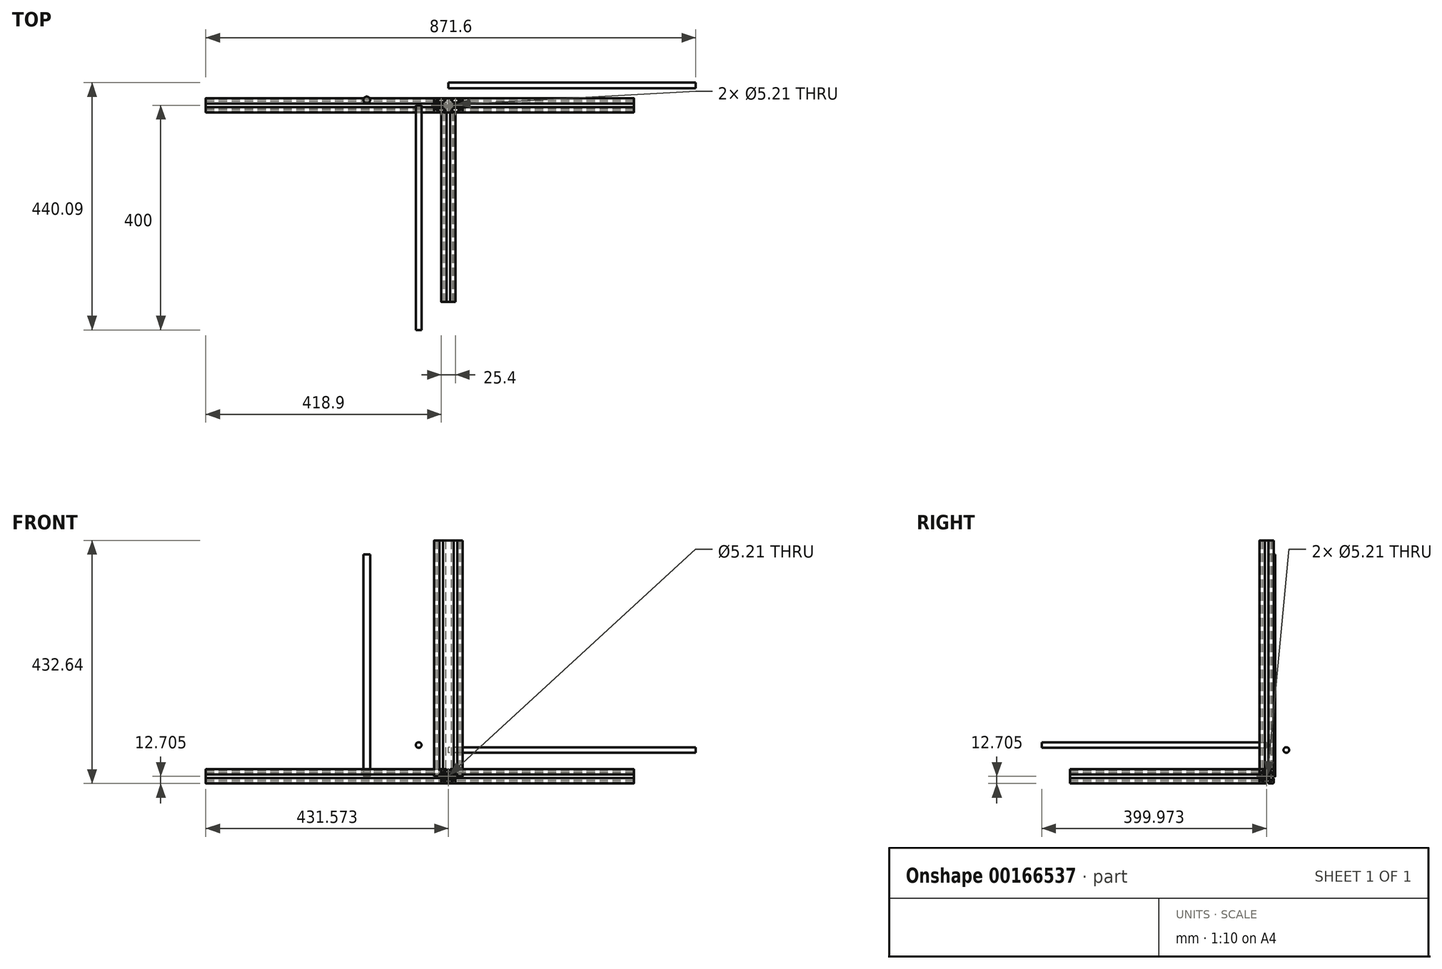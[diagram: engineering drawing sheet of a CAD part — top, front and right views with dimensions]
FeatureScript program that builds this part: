
annotation { "Feature Type Name" : "Feature", "Feature Type Description" : "" }
export const myFeature = defineFeature(function(context is Context, id is Id, definition is map)
    precondition{}
    {
        {
            assignVariable(context, id + "F0", {"name" : "Y_Extrusion_Length", "anyValue" : 350});
        }
        {
            assignVariable(context, id + "F1", {"name" : "X_Extrusion_Length", "anyValue" : 330});
        }
        {
            assignVariable(context, id + "F2", {"name" : "Z_Extrusion_Length", "anyValue" : 420});
        }
        {
            assignVariable(context, id + "F3", {"name" : "Y_Rod_Length", "anyValue" : 440});
        }
        {
            assignVariable(context, id + "F4", {"name" : "ZX_Extrusion_Length", "anyValue" : getVariable(context, 'X_Extrusion_Length') + 25.4 * 4});
        }
        {
            var Q0;
            Q0=qCreatedBy(makeId("Front.planeOp"),FACE);
            var sketch = newSketch(context, id + "F5", { "sketchPlane" : qUnion([Q0])});
            skArc(sketch, "E0", {"start": v(-10.62, 12.76) * mm, "mid": v(-12.1, 12.15) * mm, "end": v(-12.73, 10.66) * mm});
            skArc(sketch, "E1", {"start": v(-12.73, 4.4) * mm, "mid": v(-11.62, 3.3) * mm, "end": v(-10.52, 4.4) * mm});
            skArc(sketch, "E2", {"start": v(-4.37, 10.55) * mm, "mid": v(-3.27, 11.66) * mm, "end": v(-4.37, 12.76) * mm});
            skArc(sketch, "E3", {"start": v(-8.75, 7.2) * mm, "mid": v(-9.88, 7.42) * mm, "end": v(-10.52, 6.46) * mm});
            skArc(sketch, "E4", {"start": v(-6.43, 10.55) * mm, "mid": v(-7.38, 9.92) * mm, "end": v(-7.16, 8.8) * mm});
            skLineSegment(sketch, "E5", {"start": v(-12.73, 10.66) * mm, "end": v(-12.73, 4.4) * mm});
            skLineSegment(sketch, "E6", {"start": v(-10.62, 12.76) * mm, "end": v(-4.37, 12.76) * mm});
            skLineSegment(sketch, "E7", {"start": v(-10.52, 4.4) * mm, "end": v(-10.52, 6.46) * mm});
            skLineSegment(sketch, "E8", {"start": v(-4.37, 10.55) * mm, "end": v(-6.43, 10.55) * mm});
            skLineSegment(sketch, "E9", {"start": v(-11.51, 7.5) * mm, "end": v(-10.3, 7.5) * mm, "construction": true});
            skLineSegment(sketch, "E10", {"start": v(-13.64, 3.3) * mm, "end": v(-12.36, 3.3) * mm, "construction": true});
            skLineSegment(sketch, "E11", {"start": v(-7.46, 11.03) * mm, "end": v(-7.46, 8.91) * mm, "construction": true});
            skLineSegment(sketch, "E12", {"start": v(-3.27, 12.37) * mm, "end": v(-3.27, 10.25) * mm, "construction": true});
            skLineSegment(sketch, "E13.bottom", {"start": v(1.57, 4.57) * mm, "end": v(-1.63, 4.57) * mm});
            skLineSegment(sketch, "E13.top", {"start": v(1.57, -4.44) * mm, "end": v(-1.63, -4.44) * mm});
            skLineSegment(sketch, "E13.left", {"start": v(4.48, 1.66) * mm, "end": v(4.48, -1.53) * mm});
            skLineSegment(sketch, "E13.right", {"start": v(-4.54, 1.66) * mm, "end": v(-4.54, -1.53) * mm});
            skPoint(sketch, "E13.middle", {"position": v(-0.03, 0.06) * mm});
            skLineSegment(sketch, "E14", {"start": v(-8.75, 7.2) * mm, "end": v(-5.47, 3.9) * mm});
            skLineSegment(sketch, "E15", {"start": v(-7.16, 8.8) * mm, "end": v(-3.87, 5.5) * mm});
            skArc(sketch, "E16.filletArc", {"start": v(-3.87, 5.5) * mm, "mid": v(-2.84, 4.81) * mm, "end": v(-1.63, 4.57) * mm});
            skArc(sketch, "E17.filletArc", {"start": v(-4.54, 1.66) * mm, "mid": v(-4.78, 2.88) * mm, "end": v(-5.47, 3.9) * mm});
            skLineSegment(sketch, "E18", {"start": v(5.32, 0.06) * mm, "end": v(-7.21, 0.06) * mm, "construction": true});
            skPoint(sketch, "E18.startSnap0", {"position": v(2.97, 0.06) * mm});
            skPoint(sketch, "E19", {"position": v(-0.03, -4.44) * mm});
            skLineSegment(sketch, "E20", {"start": v(-0.03, -6.76) * mm, "end": v(-0.03, 5.83) * mm, "construction": true});
            skLineSegment(sketch, "E21.MirrorCS", {"start": v(11.46, 7.5) * mm, "end": v(10.25, 7.5) * mm, "construction": true});
            skArc(sketch, "E22.MirrorCS", {"start": v(10.57, 12.76) * mm, "mid": v(12.06, 12.15) * mm, "end": v(12.67, 10.66) * mm});
            skLineSegment(sketch, "E23.MirrorCS", {"start": v(7.4, 11.03) * mm, "end": v(7.4, 8.91) * mm, "construction": true});
            skLineSegment(sketch, "E24.MirrorCS", {"start": v(10.46, 4.4) * mm, "end": v(10.46, 6.46) * mm});
            skArc(sketch, "E25.MirrorCS", {"start": v(3.82, 5.5) * mm, "mid": v(2.79, 4.81) * mm, "end": v(1.57, 4.57) * mm});
            skLineSegment(sketch, "E26.MirrorCS", {"start": v(8.7, 7.2) * mm, "end": v(5.41, 3.9) * mm});
            skLineSegment(sketch, "E27.MirrorCS", {"start": v(3.21, 12.37) * mm, "end": v(3.21, 10.25) * mm, "construction": true});
            skLineSegment(sketch, "E28.MirrorCS", {"start": v(13.58, 3.3) * mm, "end": v(12.3, 3.3) * mm, "construction": true});
            skArc(sketch, "E29.MirrorCS", {"start": v(4.32, 10.55) * mm, "mid": v(3.21, 11.66) * mm, "end": v(4.32, 12.76) * mm});
            skArc(sketch, "E30.MirrorCS", {"start": v(8.7, 7.2) * mm, "mid": v(9.83, 7.42) * mm, "end": v(10.46, 6.46) * mm});
            skArc(sketch, "E31.MirrorCS", {"start": v(12.67, 4.4) * mm, "mid": v(11.57, 3.3) * mm, "end": v(10.46, 4.4) * mm});
            skLineSegment(sketch, "E32.MirrorCS", {"start": v(10.57, 12.76) * mm, "end": v(4.32, 12.76) * mm});
            skLineSegment(sketch, "E33.MirrorCS", {"start": v(12.67, 10.66) * mm, "end": v(12.67, 4.4) * mm});
            skArc(sketch, "E34.MirrorCS", {"start": v(6.37, 10.55) * mm, "mid": v(7.33, 9.92) * mm, "end": v(7.1, 8.8) * mm});
            skLineSegment(sketch, "E35.MirrorCS", {"start": v(7.1, 8.8) * mm, "end": v(3.82, 5.5) * mm});
            skLineSegment(sketch, "E36.MirrorCS", {"start": v(4.32, 10.55) * mm, "end": v(6.37, 10.55) * mm});
            skArc(sketch, "E37.MirrorCS", {"start": v(4.48, 1.66) * mm, "mid": v(4.72, 2.88) * mm, "end": v(5.41, 3.9) * mm});
            skLineSegment(sketch, "E38.MirrorCS", {"start": v(-11.51, -7.37) * mm, "end": v(-10.3, -7.37) * mm, "construction": true});
            skArc(sketch, "E39.MirrorCS", {"start": v(-3.87, -5.37) * mm, "mid": v(-2.84, -4.69) * mm, "end": v(-1.63, -4.44) * mm});
            skArc(sketch, "E40.MirrorCS", {"start": v(-10.62, -12.64) * mm, "mid": v(-12.1, -12.02) * mm, "end": v(-12.73, -10.53) * mm});
            skArc(sketch, "E41.MirrorCS", {"start": v(-8.75, -7.07) * mm, "mid": v(-9.88, -7.3) * mm, "end": v(-10.52, -6.33) * mm});
            skArc(sketch, "E42.MirrorCS", {"start": v(-6.43, -10.43) * mm, "mid": v(-7.38, -9.79) * mm, "end": v(-7.16, -8.66) * mm});
            skLineSegment(sketch, "E43.MirrorCS", {"start": v(-3.27, -12.24) * mm, "end": v(-3.27, -10.12) * mm, "construction": true});
            skArc(sketch, "E44.MirrorCS", {"start": v(-4.54, -1.53) * mm, "mid": v(-4.78, -2.75) * mm, "end": v(-5.47, -3.78) * mm});
            skLineSegment(sketch, "E45.MirrorCS", {"start": v(-12.73, -10.53) * mm, "end": v(-12.73, -4.28) * mm});
            skLineSegment(sketch, "E46.MirrorCS", {"start": v(-13.64, -3.17) * mm, "end": v(-12.36, -3.17) * mm, "construction": true});
            skLineSegment(sketch, "E47.MirrorCS", {"start": v(-7.46, -10.9) * mm, "end": v(-7.46, -8.78) * mm, "construction": true});
            skLineSegment(sketch, "E48.MirrorCS", {"start": v(-4.37, -10.43) * mm, "end": v(-6.43, -10.43) * mm});
            skLineSegment(sketch, "E49.MirrorCS", {"start": v(-10.62, -12.64) * mm, "end": v(-4.37, -12.64) * mm});
            skLineSegment(sketch, "E50.MirrorCS", {"start": v(-10.52, -4.28) * mm, "end": v(-10.52, -6.33) * mm});
            skArc(sketch, "E51.MirrorCS", {"start": v(-12.73, -4.28) * mm, "mid": v(-11.62, -3.17) * mm, "end": v(-10.52, -4.28) * mm});
            skLineSegment(sketch, "E52.MirrorCS", {"start": v(-8.75, -7.07) * mm, "end": v(-5.47, -3.78) * mm});
            skLineSegment(sketch, "E53.MirrorCS", {"start": v(-7.16, -8.66) * mm, "end": v(-3.87, -5.37) * mm});
            skArc(sketch, "E54.MirrorCS", {"start": v(-4.37, -10.43) * mm, "mid": v(-3.27, -11.53) * mm, "end": v(-4.37, -12.64) * mm});
            skLineSegment(sketch, "E55.MirrorCS", {"start": v(11.46, -7.37) * mm, "end": v(10.25, -7.37) * mm, "construction": true});
            skArc(sketch, "E56.MirrorCS", {"start": v(4.32, -10.43) * mm, "mid": v(3.21, -11.53) * mm, "end": v(4.32, -12.64) * mm});
            skLineSegment(sketch, "E57.MirrorCS", {"start": v(13.58, -3.17) * mm, "end": v(12.3, -3.17) * mm, "construction": true});
            skArc(sketch, "E58.MirrorCS", {"start": v(8.7, -7.07) * mm, "mid": v(9.83, -7.3) * mm, "end": v(10.46, -6.33) * mm});
            skLineSegment(sketch, "E59.MirrorCS", {"start": v(7.1, -8.66) * mm, "end": v(3.82, -5.37) * mm});
            skLineSegment(sketch, "E60.MirrorCS", {"start": v(7.4, -10.9) * mm, "end": v(7.4, -8.78) * mm, "construction": true});
            skLineSegment(sketch, "E61.MirrorCS", {"start": v(3.21, -12.24) * mm, "end": v(3.21, -10.12) * mm, "construction": true});
            skLineSegment(sketch, "E62.MirrorCS", {"start": v(4.32, -10.43) * mm, "end": v(6.37, -10.43) * mm});
            skArc(sketch, "E63.MirrorCS", {"start": v(3.82, -5.37) * mm, "mid": v(2.79, -4.69) * mm, "end": v(1.57, -4.44) * mm});
            skArc(sketch, "E64.MirrorCS", {"start": v(10.57, -12.64) * mm, "mid": v(12.06, -12.02) * mm, "end": v(12.67, -10.53) * mm});
            skLineSegment(sketch, "E65.MirrorCS", {"start": v(10.57, -12.64) * mm, "end": v(4.32, -12.64) * mm});
            skLineSegment(sketch, "E66.MirrorCS", {"start": v(8.7, -7.07) * mm, "end": v(5.41, -3.78) * mm});
            skLineSegment(sketch, "E67.MirrorCS", {"start": v(12.67, -10.53) * mm, "end": v(12.67, -4.28) * mm});
            skArc(sketch, "E68.MirrorCS", {"start": v(12.67, -4.28) * mm, "mid": v(11.57, -3.17) * mm, "end": v(10.46, -4.28) * mm});
            skArc(sketch, "E69.MirrorCS", {"start": v(4.48, -1.53) * mm, "mid": v(4.72, -2.75) * mm, "end": v(5.41, -3.78) * mm});
            skLineSegment(sketch, "E70.MirrorCS", {"start": v(10.46, -4.28) * mm, "end": v(10.46, -6.33) * mm});
            skArc(sketch, "E71.MirrorCS", {"start": v(6.37, -10.43) * mm, "mid": v(7.33, -9.79) * mm, "end": v(7.1, -8.66) * mm});
            skCircle(sketch, "E72", {"center": v(-0.03, 0.06) * mm, "radius": 2.6 * mm});
            skSolve(sketch);
        }
        {
            var Q0;
            Q0=qSketchRegion(id+"F5",true);
            extrude(context, id + "F6", {"entities" : qUnion([Q0]), "depth" : (getVariable(context, 'Y_Extrusion_Length')) * mm});
        }
        {
            var Q0;
            Q0=qCreatedBy(makeId("Top.planeOp"),FACE);
            var sketch = newSketch(context, id + "F7", { "sketchPlane" : qUnion([Q0])});
            skCircle(sketch, "E73", {"center": v(-145.13, 9.37) * mm, "radius": 6 * mm});
            skSolve(sketch);
        }
        {
            var Q0;
            Q0=makeQuery(id+"F7.imprint","IMPRINT",FACE,{"disambiguationData":[TD([[makeQuery(id+"F7.imprint","IMPRINT",EDGE,{"derivedFrom":sQuery(id+"F7.wireOp",EDGE,"E73")}),1.0]])]});
            extrude(context, id + "F8", {"entities" : qUnion([Q0]), "depth" : 395 * mm});
        }
        {
            var Q0;
            Q0=qCreatedBy(makeId("Right.planeOp"),FACE);
            var sketch = newSketch(context, id + "F9", { "sketchPlane" : qUnion([Q0])});
            skCircle(sketch, "E74", {"center": v(35.09, 47.05) * mm, "radius": 5 * mm});
            skSolve(sketch);
        }
        {
            var Q0;
            Q0=makeQuery(id+"F9.imprint","IMPRINT",FACE,{"disambiguationData":[TD([[makeQuery(id+"F9.imprint","IMPRINT",EDGE,{"derivedFrom":sQuery(id+"F9.wireOp",EDGE,"E74")}),1.0]])]});
            extrude(context, id + "F10", {"entities" : qUnion([Q0]), "depth" : (getVariable(context, 'Y_Rod_Length')) * mm});
        }
        {
            var Q0;
            Q0=qCreatedBy(makeId("Front.planeOp"),FACE);
            var sketch = newSketch(context, id + "F11", { "sketchPlane" : qUnion([Q0])});
            skCircle(sketch, "E75", {"center": v(-52.77, 55.86) * mm, "radius": 5 * mm});
            skSolve(sketch);
        }
        {
            var Q0;
            Q0=makeQuery(id+"F11.imprint","IMPRINT",FACE,{"disambiguationData":[TD([[makeQuery(id+"F11.imprint","IMPRINT",EDGE,{"derivedFrom":sQuery(id+"F11.wireOp",EDGE,"E75")}),1.0]])]});
            extrude(context, id + "F12", {"entities" : qUnion([Q0]), "depth" : 400 * mm});
        }
        {
            var Q0;
            Q0=qCreatedBy(makeId("Right.planeOp"),FACE);
            var sketch = newSketch(context, id + "F13", { "sketchPlane" : qUnion([Q0])});
            skArc(sketch, "E76", {"start": v(-10.62, 12.76) * mm, "mid": v(-12.1, 12.15) * mm, "end": v(-12.73, 10.66) * mm});
            skArc(sketch, "E77", {"start": v(-12.73, 4.4) * mm, "mid": v(-11.62, 3.3) * mm, "end": v(-10.52, 4.4) * mm});
            skArc(sketch, "E78", {"start": v(-4.37, 10.55) * mm, "mid": v(-3.27, 11.66) * mm, "end": v(-4.37, 12.76) * mm});
            skArc(sketch, "E79", {"start": v(-8.75, 7.2) * mm, "mid": v(-9.88, 7.42) * mm, "end": v(-10.52, 6.46) * mm});
            skArc(sketch, "E80", {"start": v(-6.43, 10.55) * mm, "mid": v(-7.38, 9.92) * mm, "end": v(-7.16, 8.8) * mm});
            skLineSegment(sketch, "E81", {"start": v(-12.73, 10.66) * mm, "end": v(-12.73, 4.4) * mm});
            skLineSegment(sketch, "E82", {"start": v(-10.62, 12.76) * mm, "end": v(-4.37, 12.76) * mm});
            skLineSegment(sketch, "E83", {"start": v(-10.52, 4.4) * mm, "end": v(-10.52, 6.46) * mm});
            skLineSegment(sketch, "E84", {"start": v(-4.37, 10.55) * mm, "end": v(-6.43, 10.55) * mm});
            skLineSegment(sketch, "E85", {"start": v(-11.51, 7.5) * mm, "end": v(-10.3, 7.5) * mm, "construction": true});
            skLineSegment(sketch, "E86", {"start": v(-13.64, 3.3) * mm, "end": v(-12.36, 3.3) * mm, "construction": true});
            skLineSegment(sketch, "E87", {"start": v(-7.46, 11.03) * mm, "end": v(-7.46, 8.91) * mm, "construction": true});
            skLineSegment(sketch, "E88", {"start": v(-3.27, 12.37) * mm, "end": v(-3.27, 10.25) * mm, "construction": true});
            skLineSegment(sketch, "E89.bottom", {"start": v(1.57, 4.57) * mm, "end": v(-1.63, 4.57) * mm});
            skLineSegment(sketch, "E89.top", {"start": v(1.57, -4.44) * mm, "end": v(-1.63, -4.44) * mm});
            skLineSegment(sketch, "E89.left", {"start": v(4.48, 1.66) * mm, "end": v(4.48, -1.53) * mm});
            skLineSegment(sketch, "E89.right", {"start": v(-4.54, 1.66) * mm, "end": v(-4.54, -1.53) * mm});
            skPoint(sketch, "E89.middle", {"position": v(-0.03, 0.06) * mm});
            skLineSegment(sketch, "E90", {"start": v(-8.75, 7.2) * mm, "end": v(-5.47, 3.9) * mm});
            skLineSegment(sketch, "E91", {"start": v(-7.16, 8.8) * mm, "end": v(-3.87, 5.5) * mm});
            skArc(sketch, "E92.filletArc", {"start": v(-3.87, 5.5) * mm, "mid": v(-2.84, 4.81) * mm, "end": v(-1.63, 4.57) * mm});
            skArc(sketch, "E93.filletArc", {"start": v(-4.54, 1.66) * mm, "mid": v(-4.78, 2.88) * mm, "end": v(-5.47, 3.9) * mm});
            skLineSegment(sketch, "E94", {"start": v(5.32, 0.06) * mm, "end": v(-7.21, 0.06) * mm, "construction": true});
            skPoint(sketch, "E94.startSnap0", {"position": v(2.97, 0.06) * mm});
            skPoint(sketch, "E95", {"position": v(-0.03, -4.44) * mm});
            skLineSegment(sketch, "E96", {"start": v(-0.03, -6.76) * mm, "end": v(-0.03, 5.83) * mm, "construction": true});
            skLineSegment(sketch, "E97.MirrorCS", {"start": v(11.46, 7.5) * mm, "end": v(10.25, 7.5) * mm, "construction": true});
            skArc(sketch, "E98.MirrorCS", {"start": v(10.57, 12.76) * mm, "mid": v(12.06, 12.15) * mm, "end": v(12.67, 10.66) * mm});
            skLineSegment(sketch, "E99.MirrorCS", {"start": v(7.4, 11.03) * mm, "end": v(7.4, 8.91) * mm, "construction": true});
            skLineSegment(sketch, "E100.MirrorCS", {"start": v(10.46, 4.4) * mm, "end": v(10.46, 6.46) * mm});
            skArc(sketch, "E101.MirrorCS", {"start": v(3.82, 5.5) * mm, "mid": v(2.79, 4.81) * mm, "end": v(1.57, 4.57) * mm});
            skLineSegment(sketch, "E102.MirrorCS", {"start": v(8.7, 7.2) * mm, "end": v(5.41, 3.9) * mm});
            skLineSegment(sketch, "E103.MirrorCS", {"start": v(3.21, 12.37) * mm, "end": v(3.21, 10.25) * mm, "construction": true});
            skLineSegment(sketch, "E104.MirrorCS", {"start": v(13.58, 3.3) * mm, "end": v(12.3, 3.3) * mm, "construction": true});
            skArc(sketch, "E105.MirrorCS", {"start": v(4.32, 10.55) * mm, "mid": v(3.21, 11.66) * mm, "end": v(4.32, 12.76) * mm});
            skArc(sketch, "E106.MirrorCS", {"start": v(8.7, 7.2) * mm, "mid": v(9.83, 7.42) * mm, "end": v(10.46, 6.46) * mm});
            skArc(sketch, "E107.MirrorCS", {"start": v(12.67, 4.4) * mm, "mid": v(11.57, 3.3) * mm, "end": v(10.46, 4.4) * mm});
            skLineSegment(sketch, "E108.MirrorCS", {"start": v(10.57, 12.76) * mm, "end": v(4.32, 12.76) * mm});
            skLineSegment(sketch, "E109.MirrorCS", {"start": v(12.67, 10.66) * mm, "end": v(12.67, 4.4) * mm});
            skArc(sketch, "E110.MirrorCS", {"start": v(6.37, 10.55) * mm, "mid": v(7.33, 9.92) * mm, "end": v(7.1, 8.8) * mm});
            skLineSegment(sketch, "E111.MirrorCS", {"start": v(7.1, 8.8) * mm, "end": v(3.82, 5.5) * mm});
            skLineSegment(sketch, "E112.MirrorCS", {"start": v(4.32, 10.55) * mm, "end": v(6.37, 10.55) * mm});
            skArc(sketch, "E113.MirrorCS", {"start": v(4.48, 1.66) * mm, "mid": v(4.72, 2.88) * mm, "end": v(5.41, 3.9) * mm});
            skLineSegment(sketch, "E114.MirrorCS", {"start": v(-11.51, -7.37) * mm, "end": v(-10.3, -7.37) * mm, "construction": true});
            skArc(sketch, "E115.MirrorCS", {"start": v(-3.87, -5.37) * mm, "mid": v(-2.84, -4.69) * mm, "end": v(-1.63, -4.44) * mm});
            skArc(sketch, "E116.MirrorCS", {"start": v(-10.62, -12.64) * mm, "mid": v(-12.1, -12.02) * mm, "end": v(-12.73, -10.53) * mm});
            skArc(sketch, "E117.MirrorCS", {"start": v(-8.75, -7.07) * mm, "mid": v(-9.88, -7.3) * mm, "end": v(-10.52, -6.33) * mm});
            skArc(sketch, "E118.MirrorCS", {"start": v(-6.43, -10.43) * mm, "mid": v(-7.38, -9.79) * mm, "end": v(-7.16, -8.66) * mm});
            skLineSegment(sketch, "E119.MirrorCS", {"start": v(-3.27, -12.24) * mm, "end": v(-3.27, -10.12) * mm, "construction": true});
            skArc(sketch, "E120.MirrorCS", {"start": v(-4.54, -1.53) * mm, "mid": v(-4.78, -2.75) * mm, "end": v(-5.47, -3.78) * mm});
            skLineSegment(sketch, "E121.MirrorCS", {"start": v(-12.73, -10.53) * mm, "end": v(-12.73, -4.28) * mm});
            skLineSegment(sketch, "E122.MirrorCS", {"start": v(-13.64, -3.17) * mm, "end": v(-12.36, -3.17) * mm, "construction": true});
            skLineSegment(sketch, "E123.MirrorCS", {"start": v(-7.46, -10.9) * mm, "end": v(-7.46, -8.78) * mm, "construction": true});
            skLineSegment(sketch, "E124.MirrorCS", {"start": v(-4.37, -10.43) * mm, "end": v(-6.43, -10.43) * mm});
            skLineSegment(sketch, "E125.MirrorCS", {"start": v(-10.62, -12.64) * mm, "end": v(-4.37, -12.64) * mm});
            skLineSegment(sketch, "E126.MirrorCS", {"start": v(-10.52, -4.28) * mm, "end": v(-10.52, -6.33) * mm});
            skArc(sketch, "E127.MirrorCS", {"start": v(-12.73, -4.28) * mm, "mid": v(-11.62, -3.17) * mm, "end": v(-10.52, -4.28) * mm});
            skLineSegment(sketch, "E128.MirrorCS", {"start": v(-8.75, -7.07) * mm, "end": v(-5.47, -3.78) * mm});
            skLineSegment(sketch, "E129.MirrorCS", {"start": v(-7.16, -8.66) * mm, "end": v(-3.87, -5.37) * mm});
            skArc(sketch, "E130.MirrorCS", {"start": v(-4.37, -10.43) * mm, "mid": v(-3.27, -11.53) * mm, "end": v(-4.37, -12.64) * mm});
            skLineSegment(sketch, "E131.MirrorCS", {"start": v(11.46, -7.37) * mm, "end": v(10.25, -7.37) * mm, "construction": true});
            skArc(sketch, "E132.MirrorCS", {"start": v(4.32, -10.43) * mm, "mid": v(3.21, -11.53) * mm, "end": v(4.32, -12.64) * mm});
            skLineSegment(sketch, "E133.MirrorCS", {"start": v(13.58, -3.17) * mm, "end": v(12.3, -3.17) * mm, "construction": true});
            skArc(sketch, "E134.MirrorCS", {"start": v(8.7, -7.07) * mm, "mid": v(9.83, -7.3) * mm, "end": v(10.46, -6.33) * mm});
            skLineSegment(sketch, "E135.MirrorCS", {"start": v(7.1, -8.66) * mm, "end": v(3.82, -5.37) * mm});
            skLineSegment(sketch, "E136.MirrorCS", {"start": v(7.4, -10.9) * mm, "end": v(7.4, -8.78) * mm, "construction": true});
            skLineSegment(sketch, "E137.MirrorCS", {"start": v(3.21, -12.24) * mm, "end": v(3.21, -10.12) * mm, "construction": true});
            skLineSegment(sketch, "E138.MirrorCS", {"start": v(4.32, -10.43) * mm, "end": v(6.37, -10.43) * mm});
            skArc(sketch, "E139.MirrorCS", {"start": v(3.82, -5.37) * mm, "mid": v(2.79, -4.69) * mm, "end": v(1.57, -4.44) * mm});
            skArc(sketch, "E140.MirrorCS", {"start": v(10.57, -12.64) * mm, "mid": v(12.06, -12.02) * mm, "end": v(12.67, -10.53) * mm});
            skLineSegment(sketch, "E141.MirrorCS", {"start": v(10.57, -12.64) * mm, "end": v(4.32, -12.64) * mm});
            skLineSegment(sketch, "E142.MirrorCS", {"start": v(8.7, -7.07) * mm, "end": v(5.41, -3.78) * mm});
            skLineSegment(sketch, "E143.MirrorCS", {"start": v(12.67, -10.53) * mm, "end": v(12.67, -4.28) * mm});
            skArc(sketch, "E144.MirrorCS", {"start": v(12.67, -4.28) * mm, "mid": v(11.57, -3.17) * mm, "end": v(10.46, -4.28) * mm});
            skArc(sketch, "E145.MirrorCS", {"start": v(4.48, -1.53) * mm, "mid": v(4.72, -2.75) * mm, "end": v(5.41, -3.78) * mm});
            skLineSegment(sketch, "E146.MirrorCS", {"start": v(10.46, -4.28) * mm, "end": v(10.46, -6.33) * mm});
            skArc(sketch, "E147.MirrorCS", {"start": v(6.37, -10.43) * mm, "mid": v(7.33, -9.79) * mm, "end": v(7.1, -8.66) * mm});
            skCircle(sketch, "E148", {"center": v(-0.03, 0.06) * mm, "radius": 2.6 * mm});
            skSolve(sketch);
        }
        {
            var Q0;
            Q0=qSketchRegion(id+"F13",true);
            extrude(context, id + "F14", {"entities" : qUnion([Q0]), "depth" : (getVariable(context, 'X_Extrusion_Length')) * mm});
        }
        {
            var Q0;
            Q0=qCreatedBy(makeId("Top.planeOp"),FACE);
            var sketch = newSketch(context, id + "F15", { "sketchPlane" : qUnion([Q0])});
            skArc(sketch, "E149", {"start": v(-23.3, 12.7) * mm, "mid": v(-24.78, 12.08) * mm, "end": v(-25.4, 10.6) * mm});
            skArc(sketch, "E150", {"start": v(-25.4, 4.34) * mm, "mid": v(-24.3, 3.24) * mm, "end": v(-23.2, 4.34) * mm});
            skArc(sketch, "E151", {"start": v(-17.04, 10.5) * mm, "mid": v(-15.94, 11.6) * mm, "end": v(-17.04, 12.7) * mm});
            skArc(sketch, "E152", {"start": v(-21.43, 7.13) * mm, "mid": v(-22.55, 7.35) * mm, "end": v(-23.2, 6.4) * mm});
            skArc(sketch, "E153", {"start": v(-19.1, 10.5) * mm, "mid": v(-20.05, 9.85) * mm, "end": v(-19.83, 8.73) * mm});
            skLineSegment(sketch, "E154", {"start": v(-25.4, 10.6) * mm, "end": v(-25.4, 4.34) * mm});
            skLineSegment(sketch, "E155", {"start": v(-23.3, 12.7) * mm, "end": v(-17.04, 12.7) * mm});
            skLineSegment(sketch, "E156", {"start": v(-23.2, 4.34) * mm, "end": v(-23.2, 6.4) * mm});
            skLineSegment(sketch, "E157", {"start": v(-17.04, 10.5) * mm, "end": v(-19.1, 10.5) * mm});
            skLineSegment(sketch, "E158", {"start": v(-9.14, 7.43) * mm, "end": v(-7.92, 7.43) * mm, "construction": true});
            skLineSegment(sketch, "E159", {"start": v(-11.26, 3.24) * mm, "end": v(-9.98, 3.24) * mm, "construction": true});
            skLineSegment(sketch, "E160", {"start": v(-20.13, 8.24) * mm, "end": v(-20.13, 6.13) * mm, "construction": true});
            skLineSegment(sketch, "E161", {"start": v(-15.94, 9.58) * mm, "end": v(-15.94, 7.46) * mm, "construction": true});
            skLineSegment(sketch, "E162.bottom", {"start": v(-11.1, 4.5) * mm, "end": v(-14.3, 4.5) * mm});
            skLineSegment(sketch, "E162.top", {"start": v(-11.1, -4.5) * mm, "end": v(-14.3, -4.5) * mm});
            skLineSegment(sketch, "E162.left", {"start": v(-8.2, 1.6) * mm, "end": v(-8.2, -1.6) * mm});
            skLineSegment(sketch, "E162.right", {"start": v(-17.2, 1.6) * mm, "end": v(-17.2, -1.6) * mm});
            skPoint(sketch, "E162.middle", {"position": v(-12.7, 0) * mm});
            skLineSegment(sketch, "E163", {"start": v(-21.43, 7.13) * mm, "end": v(-18.14, 3.84) * mm});
            skLineSegment(sketch, "E164", {"start": v(-19.83, 8.73) * mm, "end": v(-16.54, 5.44) * mm});
            skArc(sketch, "E165.filletArc", {"start": v(-16.54, 5.44) * mm, "mid": v(-15.51, 4.75) * mm, "end": v(-14.3, 4.5) * mm});
            skArc(sketch, "E166.filletArc", {"start": v(-17.2, 1.6) * mm, "mid": v(-17.45, 2.81) * mm, "end": v(-18.14, 3.84) * mm});
            skLineSegment(sketch, "E167", {"start": v(-7.21, 0) * mm, "end": v(-22.59, 0) * mm, "construction": true});
            skPoint(sketch, "E167.startSnap0", {"position": v(-12.6, 0) * mm});
            skPoint(sketch, "E168", {"position": v(-12.7, -4.5) * mm});
            skLineSegment(sketch, "E169", {"start": v(-12.7, -6.76) * mm, "end": v(-12.7, 5.83) * mm, "construction": true});
            skLineSegment(sketch, "E170.MirrorCS", {"start": v(-16.26, 7.43) * mm, "end": v(-17.48, 7.43) * mm, "construction": true});
            skLineSegment(sketch, "E171.MirrorCS", {"start": v(-5.27, 8.24) * mm, "end": v(-5.27, 6.13) * mm, "construction": true});
            skArc(sketch, "E172.MirrorCS", {"start": v(-8.86, 5.44) * mm, "mid": v(-9.89, 4.75) * mm, "end": v(-11.1, 4.5) * mm});
            skLineSegment(sketch, "E173.MirrorCS", {"start": v(-9.46, 9.58) * mm, "end": v(-9.46, 7.46) * mm, "construction": true});
            skLineSegment(sketch, "E174.MirrorCS", {"start": v(-14.14, 3.24) * mm, "end": v(-15.42, 3.24) * mm, "construction": true});
            skArc(sketch, "E175.MirrorCS", {"start": v(-8.36, 10.5) * mm, "mid": v(-9.46, 11.6) * mm, "end": v(-8.36, 12.7) * mm});
            skLineSegment(sketch, "E176.MirrorCS", {"start": v(2.1, 12.7) * mm, "end": v(-8.36, 12.7) * mm});
            skArc(sketch, "E177.MirrorCS", {"start": v(-6.3, 10.5) * mm, "mid": v(-5.35, 9.85) * mm, "end": v(-5.57, 8.73) * mm});
            skLineSegment(sketch, "E178.MirrorCS", {"start": v(-5.57, 8.73) * mm, "end": v(-8.86, 5.44) * mm});
            skLineSegment(sketch, "E179.MirrorCS", {"start": v(-8.36, 10.5) * mm, "end": v(-6.3, 10.5) * mm});
            skLineSegment(sketch, "E180.MirrorCS", {"start": v(-9.14, -7.43) * mm, "end": v(-7.92, -7.43) * mm, "construction": true});
            skArc(sketch, "E181.MirrorCS", {"start": v(-16.54, -5.44) * mm, "mid": v(-15.51, -4.75) * mm, "end": v(-14.3, -4.5) * mm});
            skArc(sketch, "E182.MirrorCS", {"start": v(-23.3, -12.7) * mm, "mid": v(-24.78, -12.08) * mm, "end": v(-25.4, -10.6) * mm});
            skArc(sketch, "E183.MirrorCS", {"start": v(-21.43, -7.13) * mm, "mid": v(-22.55, -7.35) * mm, "end": v(-23.2, -6.4) * mm});
            skArc(sketch, "E184.MirrorCS", {"start": v(-19.1, -10.5) * mm, "mid": v(-20.05, -9.85) * mm, "end": v(-19.83, -8.73) * mm});
            skLineSegment(sketch, "E185.MirrorCS", {"start": v(-15.94, -9.58) * mm, "end": v(-15.94, -7.46) * mm, "construction": true});
            skArc(sketch, "E186.MirrorCS", {"start": v(-17.2, -1.6) * mm, "mid": v(-17.45, -2.81) * mm, "end": v(-18.14, -3.84) * mm});
            skLineSegment(sketch, "E187.MirrorCS", {"start": v(-25.4, -10.6) * mm, "end": v(-25.4, -4.34) * mm});
            skLineSegment(sketch, "E188.MirrorCS", {"start": v(-11.26, -3.24) * mm, "end": v(-9.98, -3.24) * mm, "construction": true});
            skLineSegment(sketch, "E189.MirrorCS", {"start": v(-20.13, -8.24) * mm, "end": v(-20.13, -6.13) * mm, "construction": true});
            skLineSegment(sketch, "E190.MirrorCS", {"start": v(-17.04, -10.5) * mm, "end": v(-19.1, -10.5) * mm});
            skLineSegment(sketch, "E191.MirrorCS", {"start": v(-23.3, -12.7) * mm, "end": v(-17.04, -12.7) * mm});
            skLineSegment(sketch, "E192.MirrorCS", {"start": v(-23.2, -4.34) * mm, "end": v(-23.2, -6.4) * mm});
            skArc(sketch, "E193.MirrorCS", {"start": v(-25.4, -4.34) * mm, "mid": v(-24.3, -3.24) * mm, "end": v(-23.2, -4.34) * mm});
            skLineSegment(sketch, "E194.MirrorCS", {"start": v(-21.43, -7.13) * mm, "end": v(-18.14, -3.84) * mm});
            skLineSegment(sketch, "E195.MirrorCS", {"start": v(-19.83, -8.73) * mm, "end": v(-16.54, -5.44) * mm});
            skArc(sketch, "E196.MirrorCS", {"start": v(-17.04, -10.5) * mm, "mid": v(-15.94, -11.6) * mm, "end": v(-17.04, -12.7) * mm});
            skLineSegment(sketch, "E197.MirrorCS", {"start": v(-16.26, -7.43) * mm, "end": v(-17.48, -7.43) * mm, "construction": true});
            skArc(sketch, "E198.MirrorCS", {"start": v(-8.36, -10.5) * mm, "mid": v(-9.46, -11.6) * mm, "end": v(-8.36, -12.7) * mm});
            skLineSegment(sketch, "E199.MirrorCS", {"start": v(-14.14, -3.24) * mm, "end": v(-15.42, -3.24) * mm, "construction": true});
            skLineSegment(sketch, "E200.MirrorCS", {"start": v(-5.57, -8.73) * mm, "end": v(-8.86, -5.44) * mm});
            skLineSegment(sketch, "E201.MirrorCS", {"start": v(-5.27, -8.24) * mm, "end": v(-5.27, -6.13) * mm, "construction": true});
            skLineSegment(sketch, "E202.MirrorCS", {"start": v(-9.46, -9.58) * mm, "end": v(-9.46, -7.46) * mm, "construction": true});
            skLineSegment(sketch, "E203.MirrorCS", {"start": v(-8.36, -10.5) * mm, "end": v(-6.3, -10.5) * mm});
            skArc(sketch, "E204.MirrorCS", {"start": v(-8.86, -5.44) * mm, "mid": v(-9.89, -4.75) * mm, "end": v(-11.1, -4.5) * mm});
            skLineSegment(sketch, "E205.MirrorCS", {"start": v(2.1, -12.7) * mm, "end": v(-8.36, -12.7) * mm});
            skLineSegment(sketch, "E206.MirrorCS", {"start": v(0, -10.6) * mm, "end": v(0, -4.34) * mm, "construction": true});
            skArc(sketch, "E207.MirrorCS", {"start": v(-6.3, -10.5) * mm, "mid": v(-5.35, -9.85) * mm, "end": v(-5.57, -8.73) * mm});
            skCircle(sketch, "E208", {"center": v(-12.7, 0) * mm, "radius": 2.6 * mm});
            skPoint(sketch, "E209.MirrorP", {"position": v(12.7, 0) * mm});
            skLineSegment(sketch, "E210.MirrorCS", {"start": v(17.04, 10.5) * mm, "end": v(19.1, 10.5) * mm});
            skLineSegment(sketch, "E211.MirrorCS", {"start": v(17.04, -10.5) * mm, "end": v(19.1, -10.5) * mm});
            skLineSegment(sketch, "E212.MirrorCS", {"start": v(11.1, 4.5) * mm, "end": v(14.3, 4.5) * mm});
            skArc(sketch, "E213.MirrorCS", {"start": v(25.4, 4.34) * mm, "mid": v(24.3, 3.24) * mm, "end": v(23.2, 4.34) * mm});
            skArc(sketch, "E214.MirrorCS", {"start": v(17.04, 10.5) * mm, "mid": v(15.94, 11.6) * mm, "end": v(17.04, 12.7) * mm});
            skArc(sketch, "E215.MirrorCS", {"start": v(6.3, -10.5) * mm, "mid": v(5.35, -9.85) * mm, "end": v(5.57, -8.73) * mm});
            skLineSegment(sketch, "E216.MirrorCS", {"start": v(16.26, -7.43) * mm, "end": v(17.48, -7.43) * mm, "construction": true});
            skArc(sketch, "E217.MirrorCS", {"start": v(21.43, 7.13) * mm, "mid": v(22.55, 7.35) * mm, "end": v(23.2, 6.4) * mm});
            skArc(sketch, "E218.MirrorCS", {"start": v(16.54, -5.44) * mm, "mid": v(15.51, -4.75) * mm, "end": v(14.3, -4.5) * mm});
            skLineSegment(sketch, "E219.MirrorCS", {"start": v(5.27, 8.24) * mm, "end": v(5.27, 6.13) * mm, "construction": true});
            skLineSegment(sketch, "E220.MirrorCS", {"start": v(23.3, -12.7) * mm, "end": v(17.04, -12.7) * mm});
            skLineSegment(sketch, "E221.MirrorCS", {"start": v(20.13, 8.24) * mm, "end": v(20.13, 6.13) * mm, "construction": true});
            skLineSegment(sketch, "E222.MirrorCS", {"start": v(15.94, 9.58) * mm, "end": v(15.94, 7.46) * mm, "construction": true});
            skArc(sketch, "E223.MirrorCS", {"start": v(8.36, -10.5) * mm, "mid": v(9.46, -11.6) * mm, "end": v(8.36, -12.7) * mm});
            skArc(sketch, "E224.MirrorCS", {"start": v(23.3, -12.7) * mm, "mid": v(24.78, -12.08) * mm, "end": v(25.4, -10.6) * mm});
            skLineSegment(sketch, "E225.MirrorCS", {"start": v(14.14, -3.24) * mm, "end": v(15.42, -3.24) * mm, "construction": true});
            skArc(sketch, "E226.MirrorCS", {"start": v(21.43, -7.13) * mm, "mid": v(22.55, -7.35) * mm, "end": v(23.2, -6.4) * mm});
            skArc(sketch, "E227.MirrorCS", {"start": v(8.86, 5.44) * mm, "mid": v(9.89, 4.75) * mm, "end": v(11.1, 4.5) * mm});
            skLineSegment(sketch, "E228.MirrorCS", {"start": v(9.46, 9.58) * mm, "end": v(9.46, 7.46) * mm, "construction": true});
            skLineSegment(sketch, "E229.MirrorCS", {"start": v(23.2, -4.34) * mm, "end": v(23.2, -6.4) * mm});
            skLineSegment(sketch, "E230.MirrorCS", {"start": v(15.94, -9.58) * mm, "end": v(15.94, -7.46) * mm, "construction": true});
            skArc(sketch, "E231.MirrorCS", {"start": v(19.1, -10.5) * mm, "mid": v(20.05, -9.85) * mm, "end": v(19.83, -8.73) * mm});
            skLineSegment(sketch, "E232.MirrorCS", {"start": v(5.57, 8.73) * mm, "end": v(8.86, 5.44) * mm});
            skLineSegment(sketch, "E233.MirrorCS", {"start": v(7.21, 0) * mm, "end": v(22.59, 0) * mm, "construction": true});
            skArc(sketch, "E234.MirrorCS", {"start": v(25.4, -4.34) * mm, "mid": v(24.3, -3.24) * mm, "end": v(23.2, -4.34) * mm});
            skLineSegment(sketch, "E235.MirrorCS", {"start": v(8.36, 10.5) * mm, "end": v(6.3, 10.5) * mm});
            skLineSegment(sketch, "E236.MirrorCS", {"start": v(12.7, -6.76) * mm, "end": v(12.7, 5.83) * mm, "construction": true});
            skLineSegment(sketch, "E237.MirrorCS", {"start": v(25.4, -10.6) * mm, "end": v(25.4, -4.34) * mm});
            skLineSegment(sketch, "E238.MirrorCS", {"start": v(9.14, -7.43) * mm, "end": v(7.92, -7.43) * mm, "construction": true});
            skArc(sketch, "E239.MirrorCS", {"start": v(8.86, -5.44) * mm, "mid": v(9.89, -4.75) * mm, "end": v(11.1, -4.5) * mm});
            skLineSegment(sketch, "E240.MirrorCS", {"start": v(16.26, 7.43) * mm, "end": v(17.48, 7.43) * mm, "construction": true});
            skLineSegment(sketch, "E241.MirrorCS", {"start": v(11.26, -3.24) * mm, "end": v(9.98, -3.24) * mm, "construction": true});
            skLineSegment(sketch, "E242.MirrorCS", {"start": v(8.36, -10.5) * mm, "end": v(6.3, -10.5) * mm});
            skLineSegment(sketch, "E243.MirrorCS", {"start": v(21.43, -7.13) * mm, "end": v(18.14, -3.84) * mm});
            skLineSegment(sketch, "E244.MirrorCS", {"start": v(9.46, -9.58) * mm, "end": v(9.46, -7.46) * mm, "construction": true});
            skLineSegment(sketch, "E245.MirrorCS", {"start": v(14.14, 3.24) * mm, "end": v(15.42, 3.24) * mm, "construction": true});
            skArc(sketch, "E246.MirrorCS", {"start": v(17.2, 1.6) * mm, "mid": v(17.45, 2.81) * mm, "end": v(18.14, 3.84) * mm});
            skCircle(sketch, "E247.MirrorC", {"center": v(12.7, 0) * mm, "radius": 2.6 * mm});
            skLineSegment(sketch, "E248.MirrorCS", {"start": v(2.1, -12.7) * mm, "end": v(8.36, -12.7) * mm});
            skLineSegment(sketch, "E249.MirrorCS", {"start": v(2.1, 12.7) * mm, "end": v(8.36, 12.7) * mm});
            skLineSegment(sketch, "E250.MirrorCS", {"start": v(20.13, -8.24) * mm, "end": v(20.13, -6.13) * mm, "construction": true});
            skLineSegment(sketch, "E251.MirrorCS", {"start": v(21.43, 7.13) * mm, "end": v(18.14, 3.84) * mm});
            skLineSegment(sketch, "E252.MirrorCS", {"start": v(19.83, -8.73) * mm, "end": v(16.54, -5.44) * mm});
            skLineSegment(sketch, "E253.MirrorCS", {"start": v(17.2, 1.6) * mm, "end": v(17.2, -1.6) * mm});
            skArc(sketch, "E254.MirrorCS", {"start": v(8.36, 10.5) * mm, "mid": v(9.46, 11.6) * mm, "end": v(8.36, 12.7) * mm});
            skPoint(sketch, "E255.MirrorP", {"position": v(12.6, 0) * mm});
            skLineSegment(sketch, "E256.MirrorCS", {"start": v(5.27, -8.24) * mm, "end": v(5.27, -6.13) * mm, "construction": true});
            skArc(sketch, "E257.MirrorCS", {"start": v(17.2, -1.6) * mm, "mid": v(17.45, -2.81) * mm, "end": v(18.14, -3.84) * mm});
            skLineSegment(sketch, "E258.MirrorCS", {"start": v(5.57, -8.73) * mm, "end": v(8.86, -5.44) * mm});
            skArc(sketch, "E259.MirrorCS", {"start": v(6.3, 10.5) * mm, "mid": v(5.35, 9.85) * mm, "end": v(5.57, 8.73) * mm});
            skPoint(sketch, "E260.MirrorP", {"position": v(12.7, -4.5) * mm});
            skArc(sketch, "E261.MirrorCS", {"start": v(16.54, 5.44) * mm, "mid": v(15.51, 4.75) * mm, "end": v(14.3, 4.5) * mm});
            skLineSegment(sketch, "E262.MirrorCS", {"start": v(11.26, 3.24) * mm, "end": v(9.98, 3.24) * mm, "construction": true});
            skLineSegment(sketch, "E263.MirrorCS", {"start": v(9.14, 7.43) * mm, "end": v(7.92, 7.43) * mm, "construction": true});
            skLineSegment(sketch, "E264.MirrorCS", {"start": v(23.2, 4.34) * mm, "end": v(23.2, 6.4) * mm});
            skLineSegment(sketch, "E265.MirrorCS", {"start": v(23.3, 12.7) * mm, "end": v(17.04, 12.7) * mm});
            skLineSegment(sketch, "E266.MirrorCS", {"start": v(25.4, 10.6) * mm, "end": v(25.4, 4.34) * mm});
            skArc(sketch, "E267.MirrorCS", {"start": v(19.1, 10.5) * mm, "mid": v(20.05, 9.85) * mm, "end": v(19.83, 8.73) * mm});
            skArc(sketch, "E268.MirrorCS", {"start": v(23.3, 12.7) * mm, "mid": v(24.78, 12.08) * mm, "end": v(25.4, 10.6) * mm});
            skLineSegment(sketch, "E269.MirrorCS", {"start": v(8.2, 1.6) * mm, "end": v(8.2, -1.6) * mm});
            skLineSegment(sketch, "E270.MirrorCS", {"start": v(11.1, -4.5) * mm, "end": v(14.3, -4.5) * mm});
            skLineSegment(sketch, "E271.MirrorCS", {"start": v(19.83, 8.73) * mm, "end": v(16.54, 5.44) * mm});
            skArc(sketch, "E272.MirrorCS", {"start": v(17.04, -10.5) * mm, "mid": v(15.94, -11.6) * mm, "end": v(17.04, -12.7) * mm});
            skPoint(sketch, "E273.orphan", {"position": v(-2.1, 12.7) * mm});
            skPoint(sketch, "E274.orphan", {"position": v(-2.1, -12.7) * mm});
            skPoint(sketch, "E275", {"position": v(25.4, 12.7) * mm});
            skPoint(sketch, "E276", {"position": v(25.4, -12.7) * mm});
            skPoint(sketch, "E277", {"position": v(-25.4, -12.7) * mm});
            skPoint(sketch, "E278", {"position": v(-25.4, 12.7) * mm});
            skSolve(sketch);
        }
        {
            var Q0;
            Q0=qSketchRegion(id+"F15",true);
            extrude(context, id + "F16", {"entities" : qUnion([Q0]), "depth" : (getVariable(context, 'Z_Extrusion_Length')) * mm});
        }
        {
            var Q0;
            Q0=qSketchRegion(id+"F13",true);
            extrude(context, id + "F17", {"entities" : qUnion([Q0]), "oppositeDirection" : true, "depth" : (getVariable(context, 'ZX_Extrusion_Length')) * mm});
        }
        {
            var Q0;
            Q0=makeQuery(id+"F14.opExtrude","SWEPT_FACE",FACE,{"disambiguationData":[OSD([sQuery(id+"F13.wireOp",EDGE,"E82")])]});
            var sketch = newSketch(context, id + "F18", { "sketchPlane" : qUnion([Q0])});
            skPoint(sketch, "E279.0", {"position": v(330, 12.67) * mm});
            skPoint(sketch, "E279.1", {"position": v(330, -12.73) * mm});
            skPoint(sketch, "E280.0", {"position": v(0, -12.73) * mm});
            skPoint(sketch, "E280.1", {"position": v(0, 12.67) * mm});
            skPoint(sketch, "E281", {"position": v(165, -0.03) * mm});
            skPoint(sketch, "E282", {"position": v(80, -0.03) * mm});
            skPoint(sketch, "E283", {"position": v(250, -0.03) * mm});
            skSolve(sketch);
        }
    });
